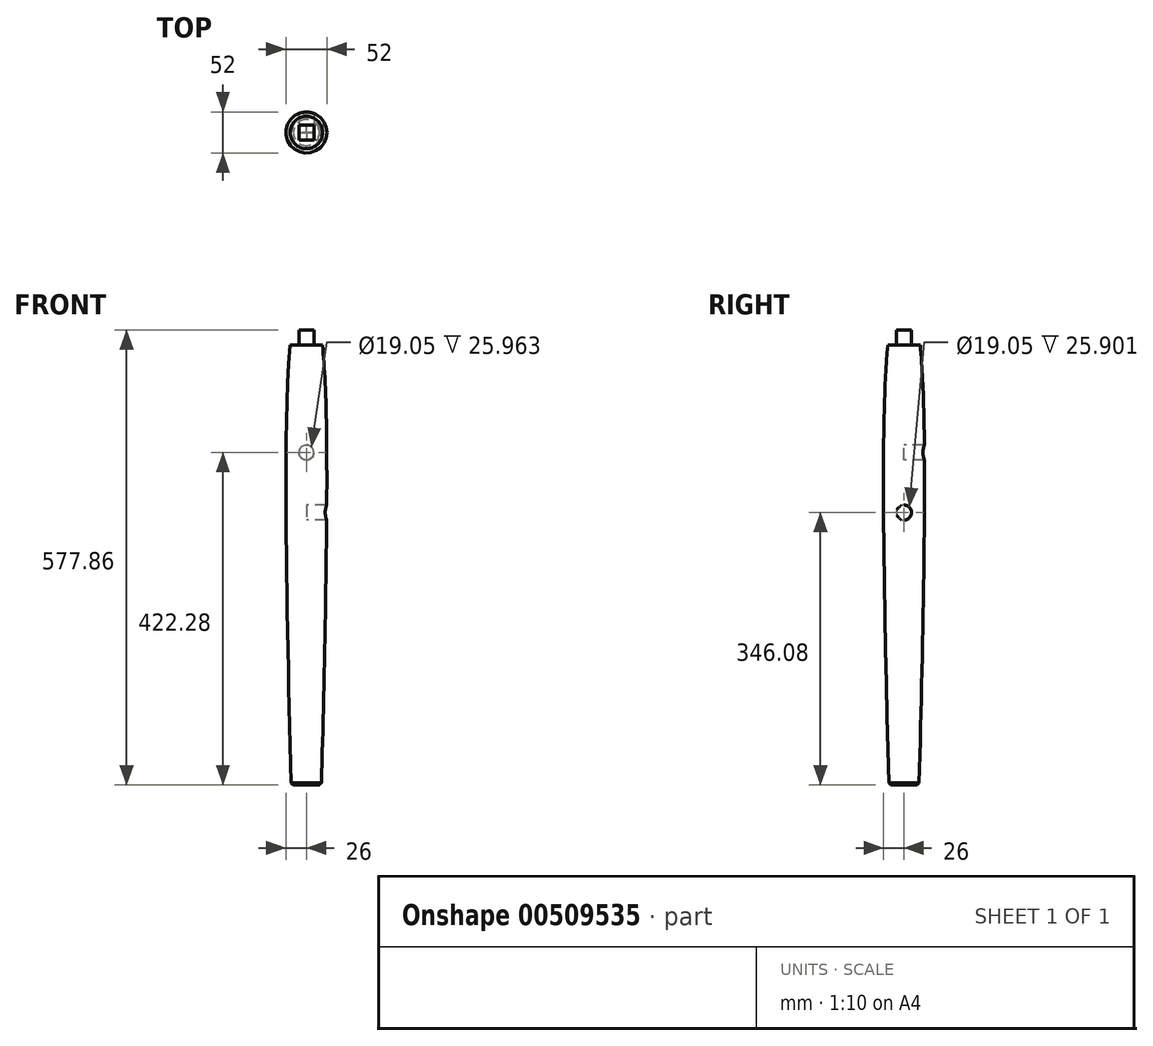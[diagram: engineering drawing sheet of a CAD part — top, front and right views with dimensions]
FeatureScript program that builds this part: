
annotation { "Feature Type Name" : "Feature", "Feature Type Description" : "" }
export const myFeature = defineFeature(function(context is Context, id is Id, definition is map)
    precondition{}
    {
        {
            var Q0;
            Q0=qCreatedBy(makeId("Front.planeOp"),FACE);
            var sketch = newSketch(context, id + "F0", { "sketchPlane" : qUnion([Q0])});
            skLineSegment(sketch, "E0", {"start": v(0, 288.92) * mm, "end": v(0, -288.92) * mm});
            skLineSegment(sketch, "E1", {"start": v(0, -288.93) * mm, "end": v(-19.05, -288.93) * mm});
            skLineSegment(sketch, "E2", {"start": v(0, 174.63) * mm, "end": v(-25.4, 174.63) * mm});
            skLineSegment(sketch, "E3", {"start": v(0, 288.93) * mm, "end": v(-19.05, 288.93) * mm});
            skFitSpline(sketch, "E4", {"points": [v(-19.05, 288.93) * mm, v(-25.4, 174.63) * mm, v(-19.05, -288.93) * mm], "startDerivative": vector(-22.35, -270.23) * mm, "endDerivative": vector(18.69, -613.54) * mm});
            skLineSegment(sketch, "E5.MirrorCS", {"start": v(0, 288.93) * mm, "end": v(19.05, 288.93) * mm});
            skFitSpline(sketch, "E6.MirrorCS", {"points": [v(19.05, 288.93) * mm, v(25.4, 174.63) * mm, v(19.05, -288.93) * mm], "startDerivative": vector(22.35, -270.23) * mm, "endDerivative": vector(-18.69, -613.54) * mm});
            skLineSegment(sketch, "E7.MirrorCS", {"start": v(0, -288.93) * mm, "end": v(19.05, -288.93) * mm});
            skSolve(sketch);
        }
        {
            var Q0;
            {var subQ0=sQuery(id+"F0.wireOp",EDGE,"E5.MirrorCS");Q0=makeQuery(id+"F0.imprint","IMPRINT",FACE,{"disambiguationData":[TD([[makeQuery(id+"F0.imprint","IMPRINT",EDGE,{"derivedFrom":subQ0}),-1.0]])]});}
            var Q1;
            Q1=sQuery(id+"F0.wireOp",EDGE,"E0");
            revolve(context, id + "F1", {"entities" : qUnion([Q0]), "axis" : qUnion([Q1]), "revolveType" : RevolveType.FULL});
        }
        {
            var Q0;
            Q0=makeQuery(id+"F1.opRevolve","SWEPT_FACE",FACE,{"disambiguationData":[OSD([sQuery(id+"F0.wireOp",EDGE,"E5.MirrorCS")])]});
            var sketch = newSketch(context, id + "F2", { "sketchPlane" : qUnion([Q0])});
            skLineSegment(sketch, "E8.bottom", {"start": v(-9.53, 9.53) * mm, "end": v(9.53, 9.53) * mm});
            skLineSegment(sketch, "E8.top", {"start": v(-9.53, -9.53) * mm, "end": v(9.53, -9.53) * mm});
            skLineSegment(sketch, "E8.left", {"start": v(-9.53, 9.53) * mm, "end": v(-9.53, -9.53) * mm});
            skLineSegment(sketch, "E8.right", {"start": v(9.53, 9.53) * mm, "end": v(9.53, -9.53) * mm});
            skPoint(sketch, "E8.middle", {"position": v(0, 0) * mm});
            skLineSegment(sketch, "E9.bottom", {"start": v(-25.4, 25.4) * mm, "end": v(25.4, 25.4) * mm});
            skLineSegment(sketch, "E9.top", {"start": v(-25.4, -25.4) * mm, "end": v(25.4, -25.4) * mm});
            skLineSegment(sketch, "E9.left", {"start": v(-25.4, 25.4) * mm, "end": v(-25.4, -25.4) * mm});
            skLineSegment(sketch, "E9.right", {"start": v(25.4, 25.4) * mm, "end": v(25.4, -25.4) * mm});
            skSolve(sketch);
        }
        {
            var Q0;
            Q0=makeQuery(id+"F2.imprint","IMPRINT",FACE,{"disambiguationData":[TD([[makeQuery(id+"F2.imprint","IMPRINT",EDGE,{"derivedFrom":sQuery(id+"F2.wireOp",EDGE,"E8.bottom")}),1.0]])]});
            var Q1;
            Q1=makeQuery(id+"F2.imprint","IMPRINT",FACE,{"disambiguationData":[TD([[makeQuery(id+"F2.imprint","IMPRINT",EDGE,{"derivedFrom":sQuery(id+"F2.wireOp",EDGE,"E9.bottom")}),-1.0]])]});
            extrude(context, id + "F3", {"entities" : qUnion([Q0, Q1]), "operationType" : NewBodyOperationType.REMOVE, "oppositeDirection" : true, "depth" : 19.05 * mm, "offsetDistance" : 25.4 * mm});
        }
        {
            var Q0;
            Q0=makeQuery(id+"F1.opRevolve","SWEPT_FACE",FACE,{"disambiguationData":[OSD([sQuery(id+"F0.wireOp",EDGE,"E7.MirrorCS")])]});
            chamfer(context, id + "F4", {"entities" : qUnion([Q0]), "width" : 2.54 * mm, "tangentPropagation" : true});
        }
        {
            var Q0;
            Q0=qCreatedBy(makeId("Front.planeOp"),FACE);
            var sketch = newSketch(context, id + "F5", { "sketchPlane" : qUnion([Q0])});
            skCircle(sketch, "E10", {"center": v(0, 133.35) * mm, "radius": 9.53 * mm});
            skSolve(sketch);
        }
        {
            var Q0;
            Q0=qSketchRegion(id+"F5",true);
            extrude(context, id + "F6", {"entities" : qUnion([Q0]), "operationType" : NewBodyOperationType.REMOVE, "endBound" : BoundingType.THROUGH_ALL, "oppositeDirection" : true, "depth" : 25.4 * mm});
        }
        {
            var Q0;
            Q0=qCreatedBy(makeId("Right.planeOp"),FACE);
            var sketch = newSketch(context, id + "F7", { "sketchPlane" : qUnion([Q0])});
            skCircle(sketch, "E11", {"center": v(0, 57.15) * mm, "radius": 9.53 * mm});
            skSolve(sketch);
        }
        {
            var Q0;
            Q0 = qSketchRegion(id + "F7", true);
            extrude(context, id + "F8", {"entities" : qUnion([Q0]), "operationType" : NewBodyOperationType.REMOVE, "endBound" : BoundingType.THROUGH_ALL, "depth" : 25.4 * mm});
        }
    });
